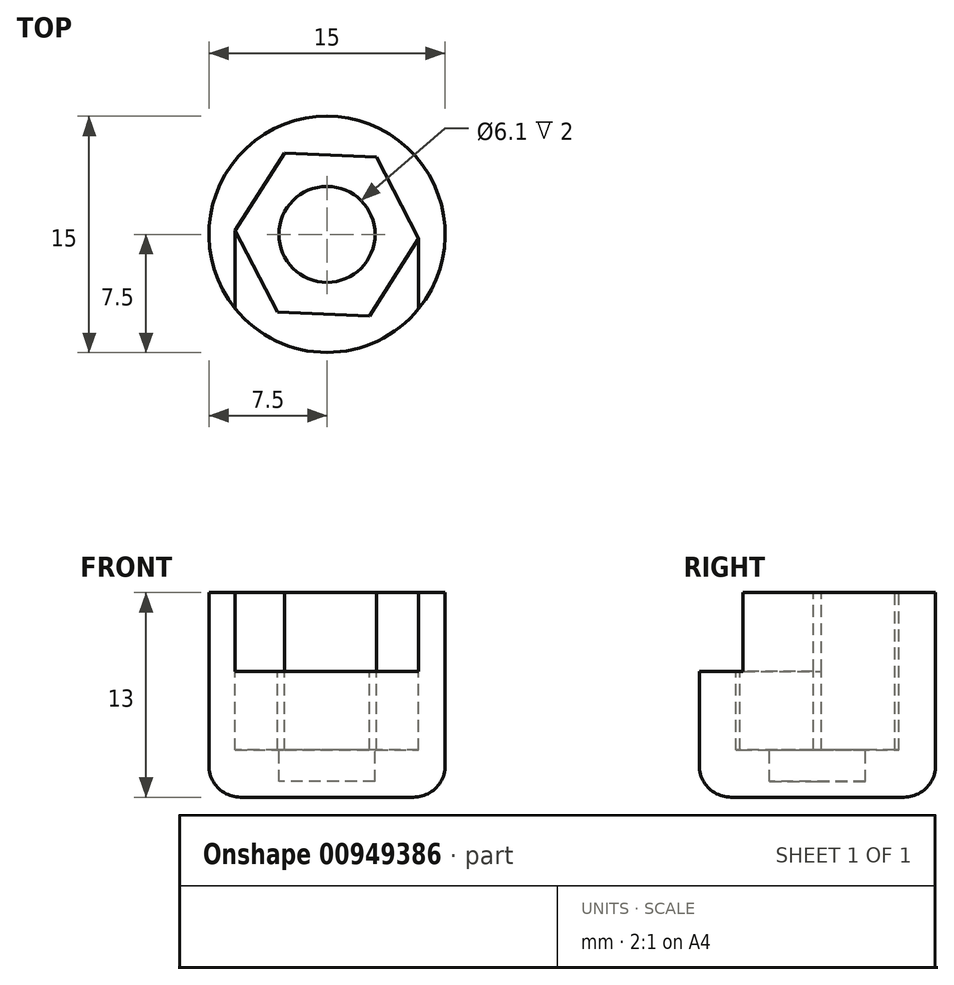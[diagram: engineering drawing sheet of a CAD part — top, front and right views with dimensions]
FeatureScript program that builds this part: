
annotation { "Feature Type Name" : "Feature", "Feature Type Description" : "" }
export const myFeature = defineFeature(function(context is Context, id is Id, definition is map)
    precondition{}
    {
        {
            var Q0;
            Q0=qCreatedBy(makeId("Top.planeOp"),FACE);
            var sketch = newSketch(context, id + "F0", { "sketchPlane" : qUnion([Q0])});
            skCircle(sketch, "E0", {"center": v(0, 0) * mm, "radius": 7.5 * mm});
            skSolve(sketch);
        }
        {
            var Q0;
            Q0 = qSketchRegion(id + "F0", true);
            extrude(context, id + "F1", {"entities" : qUnion([Q0]), "depth" : 13 * mm, "offsetDistance" : 25 * mm});
        }
        {
            var Q0;
            Q0=makeQuery(id+"F1.opExtrude","CAP_FACE",FACE,{"disambiguationData":[OSD([sQuery(id+"F0.wireOp",EDGE,"E0")])],"isStart":false});
            var sketch = newSketch(context, id + "F2", { "sketchPlane" : qUnion([Q0])});
            skCircle(sketch, "E1", {"center": v(0, 0) * mm, "radius": 3.05 * mm});
            skSolve(sketch);
        }
        {
            var Q0;
            Q0=makeQuery(id+"F2.imprint","IMPRINT",FACE,{"disambiguationData":[TD([[makeQuery(id+"F2.imprint","IMPRINT",EDGE,{"derivedFrom":sQuery(id+"F2.wireOp",EDGE,"E1")}),1.0]])]});
            extrude(context, id + "F3", {"entities" : qUnion([Q0]), "operationType" : NewBodyOperationType.REMOVE, "oppositeDirection" : true, "depth" : 12 * mm, "offsetDistance" : 25 * mm});
        }
        {
            var Q0;
            Q0=makeQuery(id+"F1.opExtrude","CAP_FACE",FACE,{"disambiguationData":[OSD([sQuery(id+"F0.wireOp",EDGE,"E0")])],"isStart":false});
            var sketch = newSketch(context, id + "F4", { "sketchPlane" : qUnion([Q0])});
            skCircle(sketch, "E2.cCircle", {"center": v(0, 0) * mm, "radius": 5.05 * mm, "construction": true});
            skLineSegment(sketch, "E2.0", {"start": v(-2.7, 5.17) * mm, "end": v(3.13, 4.92) * mm});
            skLineSegment(sketch, "E2.1", {"start": v(3.13, 4.92) * mm, "end": v(5.83, -0.25) * mm});
            skLineSegment(sketch, "E2.2", {"start": v(5.83, -0.25) * mm, "end": v(2.7, -5.17) * mm});
            skLineSegment(sketch, "E2.3", {"start": v(2.7, -5.17) * mm, "end": v(-3.13, -4.92) * mm});
            skLineSegment(sketch, "E2.4", {"start": v(-3.13, -4.92) * mm, "end": v(-5.83, 0.25) * mm});
            skLineSegment(sketch, "E2.5", {"start": v(-5.83, 0.25) * mm, "end": v(-2.7, 5.17) * mm});
            skPoint(sketch, "E2.0.midPoint", {"position": v(0.22, 5.05) * mm});
            skSolve(sketch);
        }
        {
            var Q0;
            Q0=makeQuery(id+"F4.imprint","IMPRINT",FACE,{"disambiguationData":[TD([[makeQuery(id+"F4.imprint","IMPRINT",EDGE,{"derivedFrom":sQuery(id+"F4.wireOp",EDGE,"E2.0")}),-1.0]])]});
            var sketch = newSketch(context, id + "F5", { "sketchPlane" : qUnion([Q0])});
            skSolve(sketch);
        }
        {
            var Q0;
            Q0=makeQuery(id+"F5.imprint","IMPRINT",FACE,{"disambiguationData":[TD([[makeQuery(id+"F5.imprint","IMPRINT",EDGE,{"derivedFrom":makeQuery(id+"F4.imprint","IMPRINT",EDGE,{"derivedFrom":sQuery(id+"F4.wireOp",EDGE,"E2.0")})}),-1.0]])]});
            extrude(context, id + "F6", {"entities" : qUnion([Q0]), "operationType" : NewBodyOperationType.REMOVE, "oppositeDirection" : true, "depth" : 10 * mm, "offsetDistance" : 25 * mm});
        }
        {
            var Q0;
            Q0=makeQuery(id+"F4.imprint","IMPRINT",FACE,{"disambiguationData":[TD([[makeQuery(id+"F4.imprint","IMPRINT",EDGE,{"derivedFrom":sQuery(id+"F4.wireOp",EDGE,"E2.0")}),1.0]])]});
            var sketch = newSketch(context, id + "F7", { "sketchPlane" : qUnion([Q0])});
            skLineSegment(sketch, "E3", {"start": v(-5.83, 0.25) * mm, "end": v(-5.83, -6.92) * mm});
            skLineSegment(sketch, "E4", {"start": v(5.83, -0.25) * mm, "end": v(5.83, -8.15) * mm});
            skSolve(sketch);
        }
        {
            var Q0;
            {var subQ0=makeQuery(id+"F4.imprint","IMPRINT",EDGE,{"derivedFrom":sQuery(id+"F4.wireOp",EDGE,"E2.2")});Q0=makeQuery(id+"F7.imprint","IMPRINT",FACE,{"disambiguationData":[TD([[makeQuery(id+"F7.imprint","IMPRINT",EDGE,{"derivedFrom":subQ0}),1.0]])]});}
            extrude(context, id + "F8", {"entities" : qUnion([Q0]), "operationType" : NewBodyOperationType.REMOVE, "oppositeDirection" : true, "depth" : 5 * mm, "offsetDistance" : 25 * mm});
        }
        {
            var Q0;
            Q0=makeQuery(id+"F1.opExtrude","CAP_EDGE",EDGE,{"disambiguationData":[OSD([sQuery(id+"F0.wireOp",EDGE,"E0")])],"isStart":true});
            fillet(context, id + "F9", {"entities" : qUnion([Q0]), "radius" : 2 * mm, "tangentPropagation" : true, "allowEdgeOverflow" : false});
        }
    });
